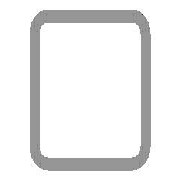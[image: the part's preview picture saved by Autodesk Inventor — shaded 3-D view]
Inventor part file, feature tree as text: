
AUTODESK INVENTOR PART (.ipt)
format: ipt  version: 2025 (Build 290162010, 162A)  size: 147,968 bytes
history: native  units: mm (DEFAULTED — no unit token found)
features: other x4, plane x3, split x2, sketch x1
ambient origin geometry x8: Origin, YZ Plane, XZ Plane, XY Plane, X Axis, Y Axis, Z Axis, Center Point
bodies: Solid1 (feature_tree), Body (feature_tree)
feature tree (10):
  parser-record x1  (decoder bookkeeping rows leaked as tree rows — omitted from the tree; the rows remain in map.json)
  other  "Driven Length"
  other  "Start Plane"
  other  "End Plane"
  plane  "Work Plane4"
  split  "Split1"
  plane  "Work Plane5"
  split  "Split2"
  sketch  "Sketch3"  dims[d3=2048.183259mm d4=0.0mm d7=4.0mm d9=40.0mm d11=40.0mm d12=2.0mm d13=56.568542mm d14=2104.751801mm d15=20.0mm d16=20.0mm d17=90.0deg d18=2048.183259mm]
  plane  "Work Plane3"
